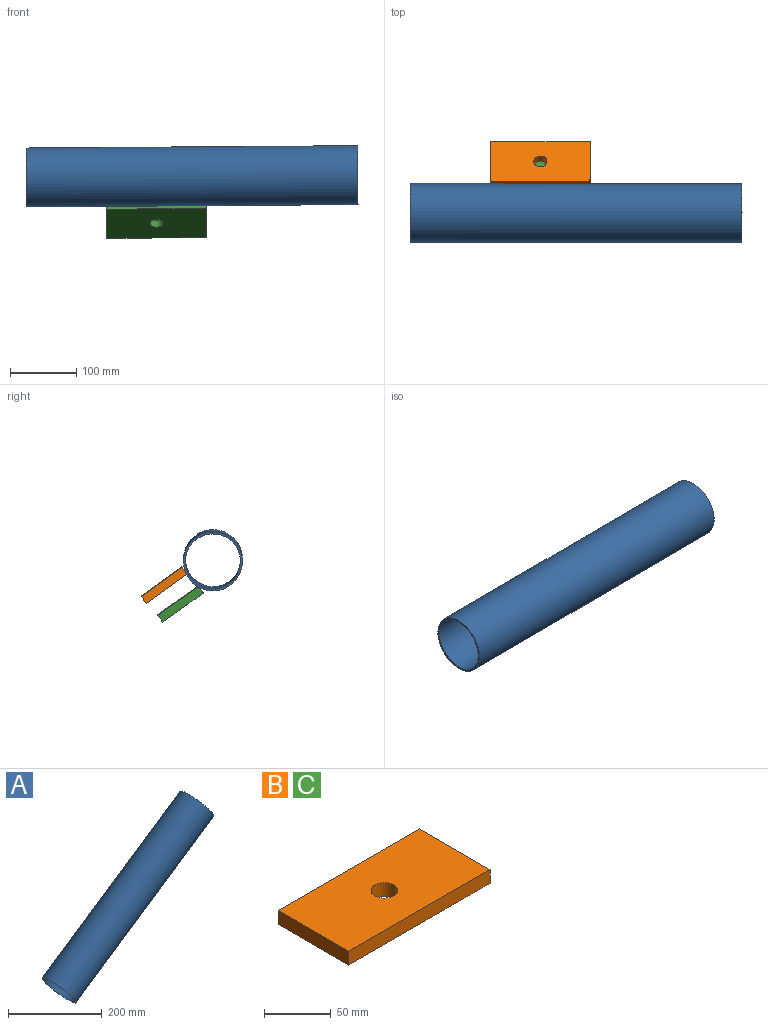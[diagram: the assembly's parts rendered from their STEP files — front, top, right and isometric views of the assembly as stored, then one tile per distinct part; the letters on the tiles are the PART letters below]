
ASSEMBLY  parts=3 mates=3
PART A: 4 faces, bbox 464.2x88.9x353.3 mm
  f0: plane 88.9x73.7mm, normal (-0.83,0,-0.56), area 809.6mm2, adj f2,f3
  f1: plane 88.9x73.7mm, normal (0.83,0,0.56), area 809.6mm2, adj f2,f3
  f2: cylinder r=44.45mm len=464.23mm, axis (0.83,0,0.56), area 139643.8mm2, adj f0,f1
  f3: cylinder r=41.45mm len=460.88mm, axis (0.83,0,0.56), area 130219mm2, adj f0,f1
PART B: 7 faces, bbox 150x75x12.7 mm
  f0: plane 150x12.7mm, normal (0,1,0), area 1905mm2, adj f1,f3,f4,f5
  f1: plane 75x12.7mm, normal (-1,0,0), area 952.5mm2, adj f0,f2,f4,f5
  f2: plane 150x12.7mm, normal (0,-1,0), area 1905mm2, adj f1,f3,f4,f5
  f3: plane 75x12.7mm, normal (1,0,0), area 952.5mm2, adj f0,f2,f4,f5
  f4: plane 150x75mm, normal (0,0,1), area 10935.8mm2, adj f0,f1,f2,f3,f6
  f5: plane 150x75mm, normal (0,0,-1), area 10935.8mm2, adj f0,f1,f2,f3,f6
  f6: cylinder r=10mm len=20mm, axis (0,0,1), area 798mm2, adj f4,f5
PART C: same geometry as B
PLACE A rot(axis=(-0.91,0.31,-0.28),88deg) t=(-249.99,84.64,-83)mm
PLACE B rot(axis=(1,0,0),144.2deg) t=(-232.96,187.43,-113.75)mm
PLACE C rot(axis=(-1,-0.01,0),35.8deg) t=(-232.73,150.12,-148.71)mm
MATE parallel B.f3 <-> A.f2  axis (1,0,0.01) through (-156.23,181.07,-116.48)mm
MATE parallel C.f5 <-> B.f4  axis (0.01,-0.58,-0.81) through (-155.84,183.11,-171.99)mm
MATE planar B.f1 <-> C.f1  axis (-1,0,-0.01) through (-306.19,177.43,-122.69)mm
